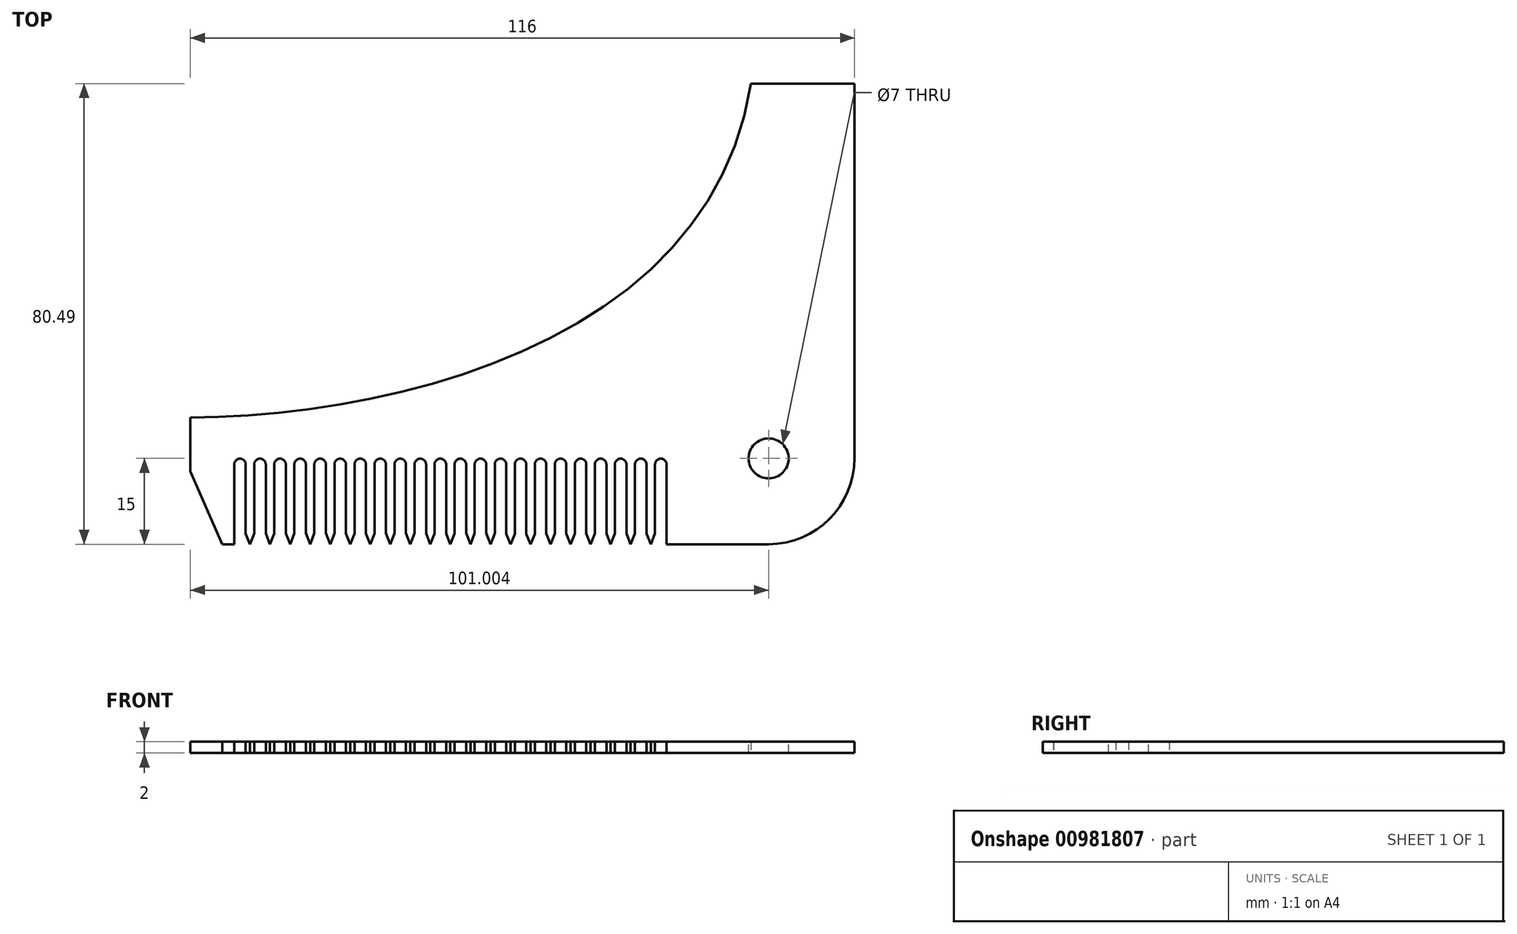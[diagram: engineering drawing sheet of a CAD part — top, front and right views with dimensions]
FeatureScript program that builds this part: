
annotation { "Feature Type Name" : "Feature", "Feature Type Description" : "" }
export const myFeature = defineFeature(function(context is Context, id is Id, definition is map)
    precondition{}
    {
        {
            var Q0;
            Q0=qCreatedBy(makeId("Top.planeOp"),FACE);
            var sketch = newSketch(context, id + "F0", { "sketchPlane" : qUnion([Q0])});
            skPoint(sketch, "E0.middle", {"position": v(0, 0) * mm});
            skLineSegment(sketch, "E1", {"start": v(-19.25, -19.04) * mm, "end": v(-19.25, -19.04) * mm});
            skLineSegment(sketch, "E2", {"start": v(-14.75, -20.04) * mm, "end": v(-14.75, -34) * mm});
            skLineSegment(sketch, "E3", {"start": v(-16.75, -20.04) * mm, "end": v(-16.75, -32.1) * mm});
            skLineSegment(sketch, "E4", {"start": v(-18.25, -20.04) * mm, "end": v(-18.25, -32.1) * mm});
            skLineSegment(sketch, "E5", {"start": v(-20.25, -20.04) * mm, "end": v(-20.25, -32.1) * mm});
            skLineSegment(sketch, "E6", {"start": v(-18.25, -32.1) * mm, "end": v(-17.5, -34) * mm});
            skLineSegment(sketch, "E7", {"start": v(-17.5, -34) * mm, "end": v(-16.75, -32.1) * mm});
            skPoint(sketch, "E8.orphan", {"position": v(-18.25, -34) * mm});
            skArc(sketch, "E9.filletArc", {"start": v(-18.25, -20.04) * mm, "mid": v(-18.54, -19.33) * mm, "end": v(-19.25, -19.04) * mm});
            skLineSegment(sketch, "E10", {"start": v(-15.75, -19.04) * mm, "end": v(-15.75, -19.04) * mm});
            skPoint(sketch, "E11.visualSharp", {"position": v(-16.75, -19.04) * mm});
            skArc(sketch, "E11.filletArc", {"start": v(-15.75, -19.04) * mm, "mid": v(-16.46, -19.33) * mm, "end": v(-16.75, -20.04) * mm});
            skPoint(sketch, "E12.visualSharp", {"position": v(-14.75, -19.04) * mm});
            skArc(sketch, "E12.filletArc", {"start": v(-14.75, -20.04) * mm, "mid": v(-15.04, -19.33) * mm, "end": v(-15.75, -19.04) * mm});
            skArc(sketch, "E13.filletArc", {"start": v(-19.25, -19.04) * mm, "mid": v(-19.96, -19.33) * mm, "end": v(-20.25, -20.04) * mm});
            skLineSegment(sketch, "E14", {"start": v(-15.75, -19.04) * mm, "end": v(-86.96, -19.04) * mm, "construction": true});
            skLineSegment(sketch, "E15", {"start": v(-21.75, -20.04) * mm, "end": v(-21.75, -32.1) * mm});
            skLineSegment(sketch, "E16", {"start": v(-23.75, -20.04) * mm, "end": v(-23.75, -32.12) * mm});
            skLineSegment(sketch, "E17", {"start": v(-21.75, -32.1) * mm, "end": v(-21, -34) * mm});
            skLineSegment(sketch, "E18", {"start": v(-21, -34) * mm, "end": v(-20.25, -32.1) * mm});
            skArc(sketch, "E19.filletArc", {"start": v(-21.75, -20.04) * mm, "mid": v(-22.04, -19.33) * mm, "end": v(-22.75, -19.04) * mm});
            skArc(sketch, "E20.filletArc", {"start": v(-22.75, -19.04) * mm, "mid": v(-23.46, -19.33) * mm, "end": v(-23.75, -20.04) * mm});
            skLineSegment(sketch, "E21", {"start": v(-25.25, -20.04) * mm, "end": v(-25.25, -32.12) * mm});
            skLineSegment(sketch, "E22", {"start": v(-27.25, -20.04) * mm, "end": v(-27.25, -32.12) * mm});
            skLineSegment(sketch, "E23", {"start": v(-25.25, -32.12) * mm, "end": v(-24.5, -34) * mm});
            skLineSegment(sketch, "E24", {"start": v(-24.5, -34) * mm, "end": v(-23.75, -32.12) * mm});
            skArc(sketch, "E25.filletArc", {"start": v(-25.25, -20.04) * mm, "mid": v(-25.54, -19.33) * mm, "end": v(-26.25, -19.04) * mm});
            skArc(sketch, "E26.filletArc", {"start": v(-26.25, -19.04) * mm, "mid": v(-26.96, -19.33) * mm, "end": v(-27.25, -20.04) * mm});
            skLineSegment(sketch, "E27", {"start": v(-28.75, -20.04) * mm, "end": v(-28.75, -32.12) * mm});
            skLineSegment(sketch, "E28", {"start": v(-28.75, -32.12) * mm, "end": v(-28, -34) * mm});
            skLineSegment(sketch, "E29", {"start": v(-28, -34) * mm, "end": v(-27.25, -32.12) * mm});
            skArc(sketch, "E30.filletArc", {"start": v(-28.75, -20.04) * mm, "mid": v(-29.04, -19.33) * mm, "end": v(-29.75, -19.04) * mm});
            skLineSegment(sketch, "E31", {"start": v(-30.75, -20.04) * mm, "end": v(-30.75, -32.15) * mm});
            skLineSegment(sketch, "E32", {"start": v(-32.25, -20.04) * mm, "end": v(-32.25, -32.15) * mm});
            skLineSegment(sketch, "E33", {"start": v(-34.25, -20.04) * mm, "end": v(-34.25, -32.15) * mm});
            skLineSegment(sketch, "E34", {"start": v(-32.25, -32.15) * mm, "end": v(-31.5, -34) * mm});
            skLineSegment(sketch, "E35", {"start": v(-31.5, -34) * mm, "end": v(-30.75, -32.15) * mm});
            skArc(sketch, "E36.filletArc", {"start": v(-32.25, -20.04) * mm, "mid": v(-32.54, -19.33) * mm, "end": v(-33.25, -19.04) * mm});
            skArc(sketch, "E37.filletArc", {"start": v(-29.75, -19.04) * mm, "mid": v(-30.46, -19.33) * mm, "end": v(-30.75, -20.04) * mm});
            skArc(sketch, "E38.filletArc", {"start": v(-33.25, -19.04) * mm, "mid": v(-33.96, -19.33) * mm, "end": v(-34.25, -20.04) * mm});
            skLineSegment(sketch, "E39", {"start": v(-35.75, -20.04) * mm, "end": v(-35.75, -32.15) * mm});
            skLineSegment(sketch, "E40", {"start": v(-37.75, -20.04) * mm, "end": v(-37.75, -32.18) * mm});
            skLineSegment(sketch, "E41", {"start": v(-35.75, -32.15) * mm, "end": v(-35, -34) * mm});
            skLineSegment(sketch, "E42", {"start": v(-35, -34) * mm, "end": v(-34.25, -32.15) * mm});
            skArc(sketch, "E43.filletArc", {"start": v(-35.75, -20.04) * mm, "mid": v(-36.04, -19.33) * mm, "end": v(-36.75, -19.04) * mm});
            skArc(sketch, "E44.filletArc", {"start": v(-36.75, -19.04) * mm, "mid": v(-37.46, -19.33) * mm, "end": v(-37.75, -20.04) * mm});
            skLineSegment(sketch, "E45", {"start": v(-39.25, -20.04) * mm, "end": v(-39.25, -32.18) * mm});
            skLineSegment(sketch, "E46", {"start": v(-41.25, -20.04) * mm, "end": v(-41.25, -32.18) * mm});
            skLineSegment(sketch, "E47", {"start": v(-39.25, -32.18) * mm, "end": v(-38.5, -34) * mm});
            skLineSegment(sketch, "E48", {"start": v(-38.5, -34) * mm, "end": v(-37.75, -32.18) * mm});
            skArc(sketch, "E49.filletArc", {"start": v(-39.25, -20.04) * mm, "mid": v(-39.54, -19.33) * mm, "end": v(-40.25, -19.04) * mm});
            skArc(sketch, "E50.filletArc", {"start": v(-40.25, -19.04) * mm, "mid": v(-40.96, -19.33) * mm, "end": v(-41.25, -20.04) * mm});
            skLineSegment(sketch, "E51", {"start": v(-42.75, -20.04) * mm, "end": v(-42.75, -32.18) * mm});
            skLineSegment(sketch, "E52", {"start": v(-42.75, -32.18) * mm, "end": v(-42, -34) * mm});
            skLineSegment(sketch, "E53", {"start": v(-42, -34) * mm, "end": v(-41.25, -32.18) * mm});
            skArc(sketch, "E54.filletArc", {"start": v(-42.75, -20.04) * mm, "mid": v(-43.04, -19.33) * mm, "end": v(-43.75, -19.04) * mm});
            skLineSegment(sketch, "E55", {"start": v(-44.75, -20.04) * mm, "end": v(-44.75, -32.07) * mm});
            skLineSegment(sketch, "E56", {"start": v(-46.25, -20.04) * mm, "end": v(-46.25, -32.07) * mm});
            skLineSegment(sketch, "E57", {"start": v(-48.25, -20.04) * mm, "end": v(-48.25, -32.07) * mm});
            skLineSegment(sketch, "E58", {"start": v(-46.25, -32.07) * mm, "end": v(-45.5, -34) * mm});
            skLineSegment(sketch, "E59", {"start": v(-45.5, -34) * mm, "end": v(-44.75, -32.07) * mm});
            skArc(sketch, "E60.filletArc", {"start": v(-46.25, -20.04) * mm, "mid": v(-46.54, -19.33) * mm, "end": v(-47.25, -19.04) * mm});
            skArc(sketch, "E61.filletArc", {"start": v(-43.75, -19.04) * mm, "mid": v(-44.46, -19.33) * mm, "end": v(-44.75, -20.04) * mm});
            skArc(sketch, "E62.filletArc", {"start": v(-47.25, -19.04) * mm, "mid": v(-47.96, -19.33) * mm, "end": v(-48.25, -20.04) * mm});
            skLineSegment(sketch, "E63", {"start": v(-49.75, -20.04) * mm, "end": v(-49.75, -32.07) * mm});
            skLineSegment(sketch, "E64", {"start": v(-51.75, -20.04) * mm, "end": v(-51.75, -32.1) * mm});
            skLineSegment(sketch, "E65", {"start": v(-49.75, -32.07) * mm, "end": v(-49, -34) * mm});
            skLineSegment(sketch, "E66", {"start": v(-49, -34) * mm, "end": v(-48.25, -32.07) * mm});
            skArc(sketch, "E67.filletArc", {"start": v(-49.75, -20.04) * mm, "mid": v(-50.04, -19.33) * mm, "end": v(-50.75, -19.04) * mm});
            skArc(sketch, "E68.filletArc", {"start": v(-50.75, -19.04) * mm, "mid": v(-51.46, -19.33) * mm, "end": v(-51.75, -20.04) * mm});
            skLineSegment(sketch, "E69", {"start": v(-53.25, -20.04) * mm, "end": v(-53.25, -32.1) * mm});
            skLineSegment(sketch, "E70", {"start": v(-55.25, -20.04) * mm, "end": v(-55.25, -32.1) * mm});
            skLineSegment(sketch, "E71", {"start": v(-53.25, -32.1) * mm, "end": v(-52.5, -34) * mm});
            skLineSegment(sketch, "E72", {"start": v(-52.5, -34) * mm, "end": v(-51.75, -32.1) * mm});
            skArc(sketch, "E73.filletArc", {"start": v(-53.25, -20.04) * mm, "mid": v(-53.54, -19.33) * mm, "end": v(-54.25, -19.04) * mm});
            skArc(sketch, "E74.filletArc", {"start": v(-54.25, -19.04) * mm, "mid": v(-54.96, -19.33) * mm, "end": v(-55.25, -20.04) * mm});
            skLineSegment(sketch, "E75", {"start": v(-56.75, -20.04) * mm, "end": v(-56.75, -32.1) * mm});
            skLineSegment(sketch, "E76", {"start": v(-56.75, -32.1) * mm, "end": v(-56, -34) * mm});
            skLineSegment(sketch, "E77", {"start": v(-56, -34) * mm, "end": v(-55.25, -32.1) * mm});
            skArc(sketch, "E78.filletArc", {"start": v(-56.75, -20.04) * mm, "mid": v(-57.04, -19.33) * mm, "end": v(-57.75, -19.04) * mm});
            skLineSegment(sketch, "E79", {"start": v(-58.75, -20.04) * mm, "end": v(-58.75, -32.07) * mm});
            skLineSegment(sketch, "E80", {"start": v(-60.25, -20.04) * mm, "end": v(-60.25, -32.07) * mm});
            skLineSegment(sketch, "E81", {"start": v(-62.25, -20.04) * mm, "end": v(-62.25, -32.07) * mm});
            skLineSegment(sketch, "E82", {"start": v(-60.25, -32.07) * mm, "end": v(-59.5, -34) * mm});
            skLineSegment(sketch, "E83", {"start": v(-59.5, -34) * mm, "end": v(-58.75, -32.07) * mm});
            skArc(sketch, "E84.filletArc", {"start": v(-60.25, -20.04) * mm, "mid": v(-60.54, -19.33) * mm, "end": v(-61.25, -19.04) * mm});
            skArc(sketch, "E85.filletArc", {"start": v(-57.75, -19.04) * mm, "mid": v(-58.46, -19.33) * mm, "end": v(-58.75, -20.04) * mm});
            skArc(sketch, "E86.filletArc", {"start": v(-61.25, -19.04) * mm, "mid": v(-61.96, -19.33) * mm, "end": v(-62.25, -20.04) * mm});
            skLineSegment(sketch, "E87", {"start": v(-63.75, -20.04) * mm, "end": v(-63.75, -32.07) * mm});
            skLineSegment(sketch, "E88", {"start": v(-65.75, -20.04) * mm, "end": v(-65.75, -32.1) * mm});
            skLineSegment(sketch, "E89", {"start": v(-63.75, -32.07) * mm, "end": v(-63, -34) * mm});
            skLineSegment(sketch, "E90", {"start": v(-63, -34) * mm, "end": v(-62.25, -32.07) * mm});
            skArc(sketch, "E91.filletArc", {"start": v(-63.75, -20.04) * mm, "mid": v(-64.04, -19.33) * mm, "end": v(-64.75, -19.04) * mm});
            skArc(sketch, "E92.filletArc", {"start": v(-64.75, -19.04) * mm, "mid": v(-65.46, -19.33) * mm, "end": v(-65.75, -20.04) * mm});
            skLineSegment(sketch, "E93", {"start": v(-67.25, -20.04) * mm, "end": v(-67.25, -32.1) * mm});
            skLineSegment(sketch, "E94", {"start": v(-69.25, -20.04) * mm, "end": v(-69.25, -32.1) * mm});
            skLineSegment(sketch, "E95", {"start": v(-67.25, -32.1) * mm, "end": v(-66.5, -34) * mm});
            skLineSegment(sketch, "E96", {"start": v(-66.5, -34) * mm, "end": v(-65.75, -32.1) * mm});
            skArc(sketch, "E97.filletArc", {"start": v(-67.25, -20.04) * mm, "mid": v(-67.54, -19.33) * mm, "end": v(-68.25, -19.04) * mm});
            skArc(sketch, "E98.filletArc", {"start": v(-68.25, -19.04) * mm, "mid": v(-68.96, -19.33) * mm, "end": v(-69.25, -20.04) * mm});
            skLineSegment(sketch, "E99", {"start": v(-70.75, -20.04) * mm, "end": v(-70.75, -32.1) * mm});
            skLineSegment(sketch, "E100", {"start": v(-70.75, -32.1) * mm, "end": v(-70, -34) * mm});
            skLineSegment(sketch, "E101", {"start": v(-70, -34) * mm, "end": v(-69.25, -32.1) * mm});
            skArc(sketch, "E102.filletArc", {"start": v(-70.75, -20.04) * mm, "mid": v(-71.04, -19.33) * mm, "end": v(-71.75, -19.04) * mm});
            skLineSegment(sketch, "E103", {"start": v(-72.75, -20.04) * mm, "end": v(-72.75, -32.07) * mm});
            skLineSegment(sketch, "E104", {"start": v(-74.25, -20.04) * mm, "end": v(-74.25, -32.07) * mm});
            skLineSegment(sketch, "E105", {"start": v(-76.25, -20.04) * mm, "end": v(-76.25, -32.07) * mm});
            skLineSegment(sketch, "E106", {"start": v(-74.25, -32.07) * mm, "end": v(-73.5, -34) * mm});
            skLineSegment(sketch, "E107", {"start": v(-73.5, -34) * mm, "end": v(-72.75, -32.07) * mm});
            skArc(sketch, "E108.filletArc", {"start": v(-74.25, -20.04) * mm, "mid": v(-74.54, -19.33) * mm, "end": v(-75.25, -19.04) * mm});
            skArc(sketch, "E109.filletArc", {"start": v(-71.75, -19.04) * mm, "mid": v(-72.46, -19.33) * mm, "end": v(-72.75, -20.04) * mm});
            skArc(sketch, "E110.filletArc", {"start": v(-75.25, -19.04) * mm, "mid": v(-75.96, -19.33) * mm, "end": v(-76.25, -20.04) * mm});
            skLineSegment(sketch, "E111", {"start": v(-77.75, -20.04) * mm, "end": v(-77.75, -32.07) * mm});
            skLineSegment(sketch, "E112", {"start": v(-79.75, -20.04) * mm, "end": v(-79.75, -32.1) * mm});
            skLineSegment(sketch, "E113", {"start": v(-77.75, -32.07) * mm, "end": v(-77, -34) * mm});
            skLineSegment(sketch, "E114", {"start": v(-77, -34) * mm, "end": v(-76.25, -32.07) * mm});
            skArc(sketch, "E115.filletArc", {"start": v(-77.75, -20.04) * mm, "mid": v(-78.04, -19.33) * mm, "end": v(-78.75, -19.04) * mm});
            skArc(sketch, "E116.filletArc", {"start": v(-78.75, -19.04) * mm, "mid": v(-79.46, -19.33) * mm, "end": v(-79.75, -20.04) * mm});
            skLineSegment(sketch, "E117", {"start": v(-81.25, -20.04) * mm, "end": v(-81.25, -32.1) * mm});
            skLineSegment(sketch, "E118", {"start": v(-81.25, -32.1) * mm, "end": v(-80.5, -34) * mm});
            skLineSegment(sketch, "E119", {"start": v(-80.5, -34) * mm, "end": v(-79.75, -32.1) * mm});
            skArc(sketch, "E120.filletArc", {"start": v(-81.25, -20.04) * mm, "mid": v(-81.54, -19.33) * mm, "end": v(-82.25, -19.04) * mm});
            skArc(sketch, "E121.filletArc", {"start": v(-82.25, -19.04) * mm, "mid": v(-82.96, -19.33) * mm, "end": v(-83.25, -20.04) * mm});
            skLineSegment(sketch, "E122.trimOffspring", {"start": v(-37.75, -34) * mm, "end": v(-37.75, -34.06) * mm});
            skPoint(sketch, "E123.orphan", {"position": v(-88.76, -34.42) * mm});
            skLineSegment(sketch, "E124", {"start": v(-83.25, -20.04) * mm, "end": v(-83.25, -32.1) * mm});
            skLineSegment(sketch, "E125", {"start": v(-84.75, -20.04) * mm, "end": v(-84.75, -32.1) * mm});
            skLineSegment(sketch, "E126", {"start": v(-86.75, -20.04) * mm, "end": v(-86.75, -32.13) * mm});
            skLineSegment(sketch, "E127", {"start": v(-84.75, -32.1) * mm, "end": v(-84, -34) * mm});
            skLineSegment(sketch, "E128", {"start": v(-84, -34) * mm, "end": v(-83.25, -32.1) * mm});
            skArc(sketch, "E129.filletArc", {"start": v(-84.75, -20.04) * mm, "mid": v(-85.04, -19.33) * mm, "end": v(-85.75, -19.04) * mm});
            skArc(sketch, "E130.filletArc", {"start": v(-85.75, -19.04) * mm, "mid": v(-86.46, -19.33) * mm, "end": v(-86.75, -20.04) * mm});
            skLineSegment(sketch, "E131", {"start": v(-88.25, -20.04) * mm, "end": v(-88.25, -32.13) * mm});
            skLineSegment(sketch, "E132", {"start": v(-88.25, -32.13) * mm, "end": v(-87.5, -34) * mm});
            skLineSegment(sketch, "E133", {"start": v(-87.5, -34) * mm, "end": v(-86.75, -32.13) * mm});
            skLineSegment(sketch, "E134", {"start": v(-90.25, -20.04) * mm, "end": v(-90.25, -32.13) * mm});
            skArc(sketch, "E135.filletArc", {"start": v(-88.25, -20.04) * mm, "mid": v(-88.54, -19.33) * mm, "end": v(-89.25, -19.04) * mm});
            skArc(sketch, "E136.filletArc", {"start": v(-89.25, -19.04) * mm, "mid": v(-89.96, -19.33) * mm, "end": v(-90.25, -20.04) * mm});
            skLineSegment(sketch, "E137", {"start": v(-14.75, -34) * mm, "end": v(-92.32, -34) * mm, "construction": true});
            skLineSegment(sketch, "E138", {"start": v(-90.25, -32.13) * mm, "end": v(-90.25, -34) * mm});
            skLineSegment(sketch, "E139", {"start": v(-97.92, -11.89) * mm, "end": v(-97.92, -21.25) * mm});
            skLineSegment(sketch, "E140", {"start": v(-97.92, -21.25) * mm, "end": v(-92.32, -34) * mm});
            skLineSegment(sketch, "E141", {"start": v(-90.25, -34) * mm, "end": v(-92.32, -34) * mm, "construction": true});
            skFitSpline(sketch, "E142", {"points": [v(-97.92, -11.89) * mm, v(0, 46.5) * mm], "startDerivative": vector(112.3, 1.03) * mm, "endDerivative": vector(20.72, 132.9) * mm});
            skLineSegment(sketch, "E143", {"start": v(0, 46.5) * mm, "end": v(18.08, 46.5) * mm});
            skLineSegment(sketch, "E144", {"start": v(18.08, 46.5) * mm, "end": v(18.08, -19) * mm});
            skLineSegment(sketch, "E145", {"start": v(-14.75, -34) * mm, "end": v(3.08, -34) * mm});
            skPoint(sketch, "E146.visualSharp", {"position": v(18.08, -34) * mm});
            skArc(sketch, "E146.filletArc", {"start": v(3.08, -34) * mm, "mid": v(13.7, -29.6) * mm, "end": v(18.08, -19) * mm});
            skLineSegment(sketch, "E147", {"start": v(-92.32, -34) * mm, "end": v(-90.25, -34) * mm});
            skSolve(sketch);
        }
        {
            var Q0;
            Q0=makeQuery(id+"F0.imprint","IMPRINT",FACE,{"disambiguationData":[TD([[makeQuery(id+"F0.imprint","IMPRINT",EDGE,{"derivedFrom":sQuery(id+"F0.wireOp",EDGE,"E0.top")}),-1.0]])]});
            var Q1;
            Q1=makeQuery(id+"F0.imprint","IMPRINT",FACE,{"disambiguationData":[TD([[makeQuery(id+"F0.imprint","IMPRINT",EDGE,{"derivedFrom":sQuery(id+"F0.wireOp",EDGE,"E2")}),1.0]])]});
            extrude(context, id + "F1", {"entities" : qUnion([Q0, Q1]), "depth" : 2 * mm, "offsetDistance" : 25 * mm});
        }
        {
            var Q0;
            Q0=makeQuery(id+"F1.opExtrude","CAP_FACE",FACE,{"disambiguationData":[OSD([sQuery(id+"F0.wireOp",EDGE,"E0.top"),sQuery(id+"F0.wireOp",EDGE,"E0.right"),sQuery(id+"F0.wireOp",EDGE,"t4YoFJ3r-Pclv-JHW4-Ga1E-XjQqiw2stvoD.bottom"),sQuery(id+"F0.wireOp",EDGE,"t4YoFJ3r-Pclv-JHW4-Ga1E-XjQqiw2stvoD.left"),sQuery(id+"F0.wireOp",EDGE,"125f6f15-feac-4c77-a320-2f7c750949d0"),sQuery(id+"F0.wireOp",EDGE,"LHh5fZmT-KsMH-d1w5-8gM1-H3SiCGTuEbTJ"),sQuery(id+"F0.wireOp",EDGE,"zO61fiIL-71c8-OjQP-pOaA-2LrEu4A94pdl"),sQuery(id+"F0.wireOp",EDGE,"E2"),sQuery(id+"F0.wireOp",EDGE,"29e26ee8-eb50-483a-b4ba-25ac74e39b51.filletArc"),sQuery(id+"F0.wireOp",EDGE,"E3"),sQuery(id+"F0.wireOp",EDGE,"E4"),sQuery(id+"F0.wireOp",EDGE,"E5"),sQuery(id+"F0.wireOp",EDGE,"E6"),sQuery(id+"F0.wireOp",EDGE,"E7"),sQuery(id+"F0.wireOp",EDGE,"E9.filletArc"),sQuery(id+"F0.wireOp",EDGE,"E11.filletArc"),sQuery(id+"F0.wireOp",EDGE,"E12.filletArc"),sQuery(id+"F0.wireOp",EDGE,"E13.filletArc"),sQuery(id+"F0.wireOp",EDGE,"E15"),sQuery(id+"F0.wireOp",EDGE,"E16"),sQuery(id+"F0.wireOp",EDGE,"E17"),sQuery(id+"F0.wireOp",EDGE,"E18"),sQuery(id+"F0.wireOp",EDGE,"E19.filletArc"),sQuery(id+"F0.wireOp",EDGE,"E20.filletArc"),sQuery(id+"F0.wireOp",EDGE,"E21"),sQuery(id+"F0.wireOp",EDGE,"E22"),sQuery(id+"F0.wireOp",EDGE,"E23"),sQuery(id+"F0.wireOp",EDGE,"E24"),sQuery(id+"F0.wireOp",EDGE,"E25.filletArc"),sQuery(id+"F0.wireOp",EDGE,"E26.filletArc"),sQuery(id+"F0.wireOp",EDGE,"E27"),sQuery(id+"F0.wireOp",EDGE,"E28"),sQuery(id+"F0.wireOp",EDGE,"E29"),sQuery(id+"F0.wireOp",EDGE,"E30.filletArc"),sQuery(id+"F0.wireOp",EDGE,"E31"),sQuery(id+"F0.wireOp",EDGE,"E32"),sQuery(id+"F0.wireOp",EDGE,"E33"),sQuery(id+"F0.wireOp",EDGE,"E34"),sQuery(id+"F0.wireOp",EDGE,"E35"),sQuery(id+"F0.wireOp",EDGE,"E36.filletArc"),sQuery(id+"F0.wireOp",EDGE,"E37.filletArc"),sQuery(id+"F0.wireOp",EDGE,"E38.filletArc"),sQuery(id+"F0.wireOp",EDGE,"E39"),sQuery(id+"F0.wireOp",EDGE,"E40"),sQuery(id+"F0.wireOp",EDGE,"E41"),sQuery(id+"F0.wireOp",EDGE,"E42"),sQuery(id+"F0.wireOp",EDGE,"E43.filletArc"),sQuery(id+"F0.wireOp",EDGE,"E44.filletArc"),sQuery(id+"F0.wireOp",EDGE,"E45"),sQuery(id+"F0.wireOp",EDGE,"E46"),sQuery(id+"F0.wireOp",EDGE,"E47"),sQuery(id+"F0.wireOp",EDGE,"E48"),sQuery(id+"F0.wireOp",EDGE,"E49.filletArc"),sQuery(id+"F0.wireOp",EDGE,"E50.filletArc"),sQuery(id+"F0.wireOp",EDGE,"E51"),sQuery(id+"F0.wireOp",EDGE,"E52"),sQuery(id+"F0.wireOp",EDGE,"E53"),sQuery(id+"F0.wireOp",EDGE,"E54.filletArc"),sQuery(id+"F0.wireOp",EDGE,"E55"),sQuery(id+"F0.wireOp",EDGE,"E56"),sQuery(id+"F0.wireOp",EDGE,"E57"),sQuery(id+"F0.wireOp",EDGE,"E58"),sQuery(id+"F0.wireOp",EDGE,"E59"),sQuery(id+"F0.wireOp",EDGE,"E60.filletArc"),sQuery(id+"F0.wireOp",EDGE,"E61.filletArc"),sQuery(id+"F0.wireOp",EDGE,"E62.filletArc"),sQuery(id+"F0.wireOp",EDGE,"E63"),sQuery(id+"F0.wireOp",EDGE,"E64"),sQuery(id+"F0.wireOp",EDGE,"E65"),sQuery(id+"F0.wireOp",EDGE,"E66"),sQuery(id+"F0.wireOp",EDGE,"E67.filletArc"),sQuery(id+"F0.wireOp",EDGE,"E68.filletArc"),sQuery(id+"F0.wireOp",EDGE,"E69"),sQuery(id+"F0.wireOp",EDGE,"E70"),sQuery(id+"F0.wireOp",EDGE,"E71"),sQuery(id+"F0.wireOp",EDGE,"E72"),sQuery(id+"F0.wireOp",EDGE,"E73.filletArc"),sQuery(id+"F0.wireOp",EDGE,"E74.filletArc"),sQuery(id+"F0.wireOp",EDGE,"E75"),sQuery(id+"F0.wireOp",EDGE,"E76"),sQuery(id+"F0.wireOp",EDGE,"E77"),sQuery(id+"F0.wireOp",EDGE,"E78.filletArc"),sQuery(id+"F0.wireOp",EDGE,"E79"),sQuery(id+"F0.wireOp",EDGE,"E80"),sQuery(id+"F0.wireOp",EDGE,"E81"),sQuery(id+"F0.wireOp",EDGE,"E82"),sQuery(id+"F0.wireOp",EDGE,"E83"),sQuery(id+"F0.wireOp",EDGE,"E84.filletArc"),sQuery(id+"F0.wireOp",EDGE,"E85.filletArc"),sQuery(id+"F0.wireOp",EDGE,"E86.filletArc"),sQuery(id+"F0.wireOp",EDGE,"E87"),sQuery(id+"F0.wireOp",EDGE,"E88"),sQuery(id+"F0.wireOp",EDGE,"E89"),sQuery(id+"F0.wireOp",EDGE,"E90"),sQuery(id+"F0.wireOp",EDGE,"E91.filletArc"),sQuery(id+"F0.wireOp",EDGE,"E92.filletArc"),sQuery(id+"F0.wireOp",EDGE,"E93"),sQuery(id+"F0.wireOp",EDGE,"E94"),sQuery(id+"F0.wireOp",EDGE,"E95"),sQuery(id+"F0.wireOp",EDGE,"E96"),sQuery(id+"F0.wireOp",EDGE,"E97.filletArc"),sQuery(id+"F0.wireOp",EDGE,"E98.filletArc"),sQuery(id+"F0.wireOp",EDGE,"E99"),sQuery(id+"F0.wireOp",EDGE,"E100"),sQuery(id+"F0.wireOp",EDGE,"E101"),sQuery(id+"F0.wireOp",EDGE,"E102.filletArc"),sQuery(id+"F0.wireOp",EDGE,"E103"),sQuery(id+"F0.wireOp",EDGE,"E104"),sQuery(id+"F0.wireOp",EDGE,"E105"),sQuery(id+"F0.wireOp",EDGE,"E106"),sQuery(id+"F0.wireOp",EDGE,"E107"),sQuery(id+"F0.wireOp",EDGE,"E108.filletArc"),sQuery(id+"F0.wireOp",EDGE,"E109.filletArc"),sQuery(id+"F0.wireOp",EDGE,"E110.filletArc"),sQuery(id+"F0.wireOp",EDGE,"E111"),sQuery(id+"F0.wireOp",EDGE,"E112"),sQuery(id+"F0.wireOp",EDGE,"E113"),sQuery(id+"F0.wireOp",EDGE,"E114"),sQuery(id+"F0.wireOp",EDGE,"E115.filletArc"),sQuery(id+"F0.wireOp",EDGE,"E116.filletArc"),sQuery(id+"F0.wireOp",EDGE,"E117"),sQuery(id+"F0.wireOp",EDGE,"9480b553-3ddc-47e3-bced-cfdf7d2bfebb"),sQuery(id+"F0.wireOp",EDGE,"E118"),sQuery(id+"F0.wireOp",EDGE,"E119"),sQuery(id+"F0.wireOp",EDGE,"E120.filletArc"),sQuery(id+"F0.wireOp",EDGE,"E121.filletArc"),sQuery(id+"F0.wireOp",EDGE,"DohBKfLT-X6Vi-FM5y-xKxJ-d1fNNuwRdMis")])],"isStart":false});
            var sketch = newSketch(context, id + "F2", { "sketchPlane" : qUnion([Q0])});
            skCircle(sketch, "E148", {"center": v(3.08, -19) * mm, "radius": 3.5 * mm});
            skSolve(sketch);
        }
        {
            var Q0;
            Q0 = qSketchRegion(id + "F2", true);
            extrude(context, id + "F3", {"entities" : qUnion([Q0]), "operationType" : NewBodyOperationType.REMOVE, "oppositeDirection" : true, "depth" : 25 * mm, "offsetDistance" : 25 * mm});
        }
    });
